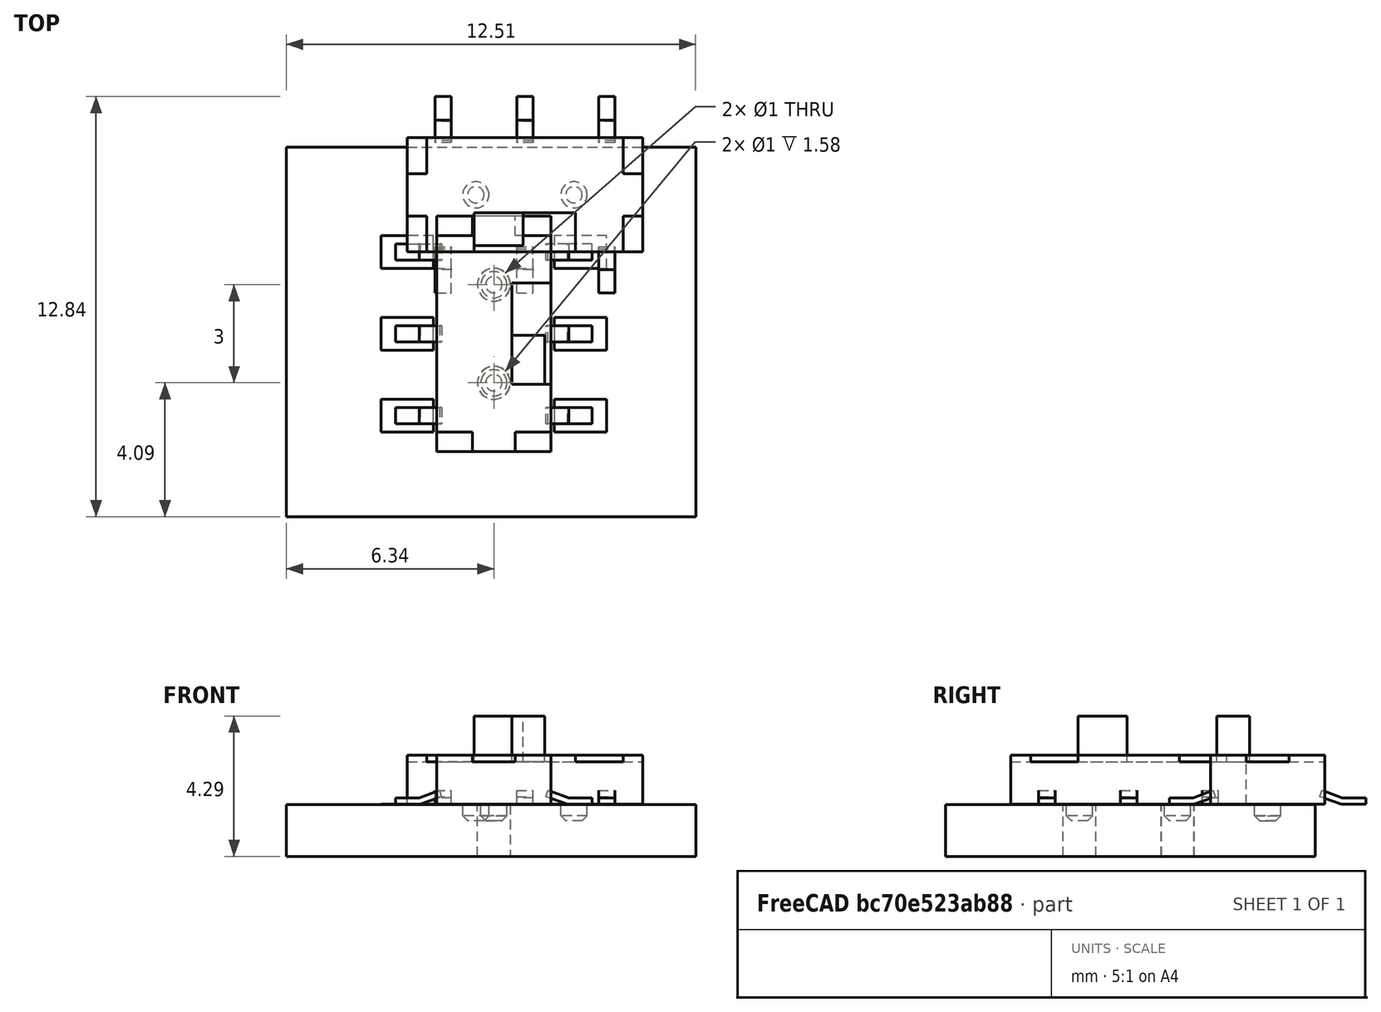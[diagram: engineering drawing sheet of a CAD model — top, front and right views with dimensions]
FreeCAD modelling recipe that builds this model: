
FCSTD DOCUMENT  (FreeCAD 0.18R16131 (Git))
Label: CK_AYZ0202AGRLC
License: All rights reserved
LicenseURL: http://en.wikipedia.org/wiki/All_rights_reserved
objects: Part::Box×26, Part::Feature×12, Part::Cut×11, Part::MultiFuse×6, Part::FeaturePython×6, Part::Cylinder×2, Part::Chamfer×2, App::Part×1, App::DocumentObjectGroup×1
note: 65 computed .brp shape members not serialized (recipe doc carries the construction recipe); baked Part::Feature solids carry a one-line shape summary decoded from their .brp

FEATURE [Part::Box] Box  label="Cube"
  AttacherType = Attacher::AttachEngine3D
  Height = 1.5
  Length = 7.2
  Width = 3.5
FEATURE [Part::Box] Box001  label="Cube001"
  AttacherType = Attacher::AttachEngine3D
  Height = 0.2
  Length = 0.5
  Placement = pos=(0,-1.25,0) rot=(0,0,1;0rad)
  Width = 0.75
FEATURE [Part::Box] Box002  label="Cube002"
  AttacherType = Attacher::AttachEngine3D
  Height = 0.2
  Length = 0.5
  Placement = pos=(0,-0.5,0) rot=(1,0,0;0.349066rad)
  Width = 0.7
FEATURE [Part::MultiFuse] Fusion  label="Pin 4"
  Placement = pos=(3.35,0,0) rot=(0,0,1;0rad)
  Shapes = -> [Box002,Box001]
FEATURE [Part::Box] Box003  label="Cube003"
  AttacherType = Attacher::AttachEngine3D
  Height = 0.2
  Length = 0.5
  Placement = pos=(0,-1.25,0) rot=(0,0,1;0rad)
  Width = 0.75
FEATURE [Part::Box] Box004  label="Cube004"
  AttacherType = Attacher::AttachEngine3D
  Height = 0.2
  Length = 0.5
  Placement = pos=(0,-0.5,0) rot=(1,0,0;0.349066rad)
  Width = 0.7
FEATURE [Part::MultiFuse] Fusion001  label="Pin 5"
  Placement = pos=(0.85,0,0) rot=(0,0,1;0rad)
  Shapes = -> [Box004,Box003]
FEATURE [Part::Box] Box005  label="Cube005"
  AttacherType = Attacher::AttachEngine3D
  Height = 0.2
  Length = 0.5
  Placement = pos=(0,-1.25,0) rot=(0,0,1;0rad)
  Width = 0.75
FEATURE [Part::Box] Box006  label="Cube006"
  AttacherType = Attacher::AttachEngine3D
  Height = 0.2
  Length = 0.5
  Placement = pos=(0,-0.5,0) rot=(1,0,0;0.349066rad)
  Width = 0.7
FEATURE [Part::MultiFuse] Fusion002  label="Pin 6"
  Placement = pos=(5.85,0,0) rot=(0,0,1;0rad)
  Shapes = -> [Box006,Box005]
FEATURE [Part::Box] Box007  label="Cube007"
  AttacherType = Attacher::AttachEngine3D
  Height = 0.2
  Length = 0.5
  Placement = pos=(0,-1.25,0) rot=(0,0,1;0rad)
  Width = 0.75
FEATURE [Part::Box] Box008  label="Cube008"
  AttacherType = Attacher::AttachEngine3D
  Height = 0.2
  Length = 0.5
  Placement = pos=(0,-0.5,0) rot=(1,0,0;0.349066rad)
  Width = 0.7
FEATURE [Part::MultiFuse] Fusion003  label="Pin 2"
  Placement = pos=(3.85,3.5,0) rot=(0,0,1;3.14159rad)
  Shapes = -> [Box008,Box007]
FEATURE [Part::Box] Box009  label="Cube009"
  AttacherType = Attacher::AttachEngine3D
  Height = 0.2
  Length = 0.5
  Placement = pos=(0,-1.25,0) rot=(0,0,1;0rad)
  Width = 0.75
FEATURE [Part::Box] Box010  label="Cube010"
  AttacherType = Attacher::AttachEngine3D
  Height = 0.2
  Length = 0.5
  Placement = pos=(0,-0.5,0) rot=(1,0,0;0.349066rad)
  Width = 0.7
FEATURE [Part::MultiFuse] Fusion004  label="Pin 1"
  Placement = pos=(1.35,3.5,0) rot=(0,0,1;3.14159rad)
  Shapes = -> [Box010,Box009]
FEATURE [Part::Box] Box011  label="Cube011"
  AttacherType = Attacher::AttachEngine3D
  Height = 0.2
  Length = 0.5
  Placement = pos=(0,-1.25,0) rot=(0,0,1;0rad)
  Width = 0.75
FEATURE [Part::Box] Box012  label="Cube012"
  AttacherType = Attacher::AttachEngine3D
  Height = 0.2
  Length = 0.5
  Placement = pos=(0,-0.5,0) rot=(1,0,0;0.349066rad)
  Width = 0.7
FEATURE [Part::MultiFuse] Fusion005  label="Pin 3"
  Placement = pos=(6.35,3.5,0) rot=(0,0,1;3.14159rad)
  Shapes = -> [Box012,Box011]
FEATURE [Part::Box] Box014  label="Cube014"
  AttacherType = Attacher::AttachEngine3D
  Height = 0.2
  Length = 0.6
  Placement = pos=(6.6,0,1.3) rot=(0,0,1;0rad)
  Width = 1.1
FEATURE [Part::Box] Box015  label="Cube015"
  AttacherType = Attacher::AttachEngine3D
  Height = 0.2
  Length = 0.6
  Placement = pos=(6.6,2.4,1.3) rot=(0,0,1;0rad)
  Width = 1.1
FEATURE [Part::Box] Box016  label="Cube016"
  AttacherType = Attacher::AttachEngine3D
  Height = 0.2
  Length = 0.6
  Placement = pos=(0,0,1.3) rot=(0,0,1;0rad)
  Width = 1.1
FEATURE [Part::Box] Box017  label="Cube017"
  AttacherType = Attacher::AttachEngine3D
  Height = 0.2
  Length = 0.6
  Placement = pos=(0,2.4,1.3) rot=(0,0,1;0rad)
  Width = 1.1
FEATURE [Part::Box] Box018  label="Cube018"
  AttacherType = Attacher::AttachEngine3D
  Height = 0.2
  Length = 3.1
  Placement = pos=(2.05,0,1.3) rot=(0,0,1;0rad)
  Width = 1.2
FEATURE [Part::Box] Box019  label="Cube019"
  AttacherType = Attacher::AttachEngine3D
  Height = 0.2
  Length = 7.2
  Placement = pos=(0,0,1.3) rot=(0,0,1;0rad)
  Width = 3.5
FEATURE [Part::Cut] Cut
  Base = -> Box019
  Tool = -> Box014
FEATURE [Part::Cut] Cut001
  Base = -> Cut
  Tool = -> Box015
FEATURE [Part::Cut] Cut002
  Base = -> Cut001
  Tool = -> Box016
FEATURE [Part::Cut] Cut003
  Base = -> Cut002
  Tool = -> Box017
FEATURE [Part::Cut] Cut004  label="Silver Top"
  Base = -> Cut003
  Tool = -> Box018
FEATURE [Part::Box] Box020  label="Cube020"
  AttacherType = Attacher::AttachEngine3D
  Height = 0.2
  Length = 0.6
  Placement = pos=(6.6,0,1.3) rot=(0,0,1;0rad)
  Width = 1.1
FEATURE [Part::Box] Box021  label="Cube021"
  AttacherType = Attacher::AttachEngine3D
  Height = 0.2
  Length = 0.6
  Placement = pos=(6.6,2.4,1.3) rot=(0,0,1;0rad)
  Width = 1.1
FEATURE [Part::Box] Box022  label="Cube022"
  AttacherType = Attacher::AttachEngine3D
  Height = 0.2
  Length = 0.6
  Placement = pos=(0,0,1.3) rot=(0,0,1;0rad)
  Width = 1.1
FEATURE [Part::Box] Box023  label="Cube023"
  AttacherType = Attacher::AttachEngine3D
  Height = 0.2
  Length = 0.6
  Placement = pos=(0,2.4,1.3) rot=(0,0,1;0rad)
  Width = 1.1
FEATURE [Part::Box] Box024  label="Cube024"
  AttacherType = Attacher::AttachEngine3D
  Height = 0.2
  Length = 3.1
  Placement = pos=(2.05,0,1.3) rot=(0,0,1;0rad)
  Width = 1.2
FEATURE [Part::Box] Box025  label="Cube025"
  AttacherType = Attacher::AttachEngine3D
  Height = 0.2
  Length = 7.2
  Placement = pos=(0,0,1.3) rot=(0,0,1;0rad)
  Width = 3.5
FEATURE [Part::Cut] Cut005
  Base = -> Box025
  Tool = -> Box020
FEATURE [Part::Cut] Cut009
  Base = -> Cut005
  Tool = -> Box021
FEATURE [Part::Cut] Cut006
  Base = -> Cut009
  Tool = -> Box022
FEATURE [Part::Cut] Cut008
  Base = -> Cut006
  Tool = -> Box023
FEATURE [Part::Cut] Cut007  label="Silver Top001"
  Base = -> Cut008
  Tool = -> Box024
FEATURE [Part::Cut] Cut010  label="Plastic Body"
  Base = -> Box
  Tool = -> Cut007
FEATURE [Part::Box] Box026  label="Cube026"
  AttacherType = Attacher::AttachEngine3D
  Height = 1.4
  Length = 1.5
  Placement = pos=(2.05,0.2,1.3) rot=(0,0,1;0rad)
  Width = 1
FEATURE [Part::Cylinder] Cylinder
  Angle = 360
  AttacherType = Attacher::AttachEngine3D
  Height = 0.5
  Placement = pos=(3.6,1.75,-0.5) rot=(0,0,1;0rad)
  Radius = 0.4
FEATURE [Part::Chamfer] Chamfer
  Base = -> Cylinder
  Edges = 1 edges r=0.15: [Edge3]
  Placement = pos=(-1.5,0,0) rot=(0,0,1;0rad)
FEATURE [Part::Cylinder] Cylinder001
  Angle = 360
  AttacherType = Attacher::AttachEngine3D
  Height = 0.5
  Placement = pos=(3.6,1.75,-0.5) rot=(0,0,1;0rad)
  Radius = 0.4
FEATURE [Part::Chamfer] Chamfer001
  Base = -> Cylinder001
  Edges = 1 edges r=0.15: [Edge3]
  Placement = pos=(1.5,0,0) rot=(0,0,1;0rad)
FEATURE [App::Part] Part
  Group = -> [Box001,Box002,Fusion,Box004,Box003,Fusion001,Box006,Box005,Fusion002,Box007,Box008,Fusion003,Box010,Box009,Fusion004,Box012,Box011,Fusion005,Cut,Cut002,Cut003,Cut001,Box014,Box015,Box016,Box017,Box018,Box019,Cut004,Cut007,Cut008,Cut009,Cut005,Cut006,Box,Box020,Box023,Box021,Box025,Box022,Box024,Cut010,Box026,Cylinder,Chamfer,Cylinder001,Chamfer001]
  Origin = -> Origin
FEATURE [Part::FeaturePython] FCrtYd_lines  label="FCrtYd"  # a2plus imported part (geometry in sourceFile) (typed FeaturePython)
  fixedPosition = true
FEATURE [Part::FeaturePython] FFab_lines  label="FFab"  # a2plus imported part (geometry in sourceFile) (typed FeaturePython)
  fixedPosition = true
FEATURE [Part::FeaturePython] Filk_lines  label="FrontSilk"  # a2plus imported part (geometry in sourceFile) (typed FeaturePython)
  fixedPosition = true
FEATURE [Part::FeaturePython] TopPads  # a2plus imported part (geometry in sourceFile) (typed FeaturePython)
  fixedPosition = true
FEATURE [Part::FeaturePython] THPs  label="PTHs"  # a2plus imported part (geometry in sourceFile) (typed FeaturePython)
  fixedPosition = true
FEATURE [Part::FeaturePython] newPCB  label="Pcb"  # a2plus imported part (geometry in sourceFile) (typed FeaturePython)
  fixedPosition = true
FEATURE [App::DocumentObjectGroup] Switch_Slide_SPDT_SMD_fp
  Group = -> [FCrtYd_lines,FFab_lines,Filk_lines,TopPads,THPs,newPCB]
FEATURE [Part::Feature] Fusion_cp  label="Pin 4_cp"
  Placement = pos=(3.35,0,0) rot=(0,0,1;0rad)
  shape: bbox 0.5 x 1.408 x 0.4274 mm, 12 faces (baked)
FEATURE [Part::Feature] Fusion001_cp  label="Pin 5_cp"
  Placement = pos=(0.85,0,0) rot=(0,0,1;0rad)
  shape: bbox 0.5 x 1.408 x 0.4274 mm, 12 faces (baked)
FEATURE [Part::Feature] Fusion002_cp  label="Pin 6_cp"
  Placement = pos=(5.85,0,0) rot=(0,0,1;0rad)
  shape: bbox 0.5 x 1.408 x 0.4274 mm, 12 faces (baked)
FEATURE [Part::Feature] Fusion003_cp  label="Pin 2_cp"
  Placement = pos=(3.85,3.5,0) rot=(0,0,1;3.14159rad)
  shape: bbox 0.5 x 1.408 x 0.4274 mm, 12 faces (baked)
FEATURE [Part::Feature] Fusion004_cp  label="Pin 1_cp"
  Placement = pos=(1.35,3.5,0) rot=(0,0,1;3.14159rad)
  shape: bbox 0.5 x 1.408 x 0.4274 mm, 12 faces (baked)
FEATURE [Part::Feature] Fusion005_cp  label="Pin 3_cp"
  Placement = pos=(6.35,3.5,0) rot=(0,0,1;3.14159rad)
  shape: bbox 0.5 x 1.408 x 0.4274 mm, 12 faces (baked)
FEATURE [Part::Feature] Cut004_cp  label="Silver Top_cp"
  shape: bbox 7.2 x 3.5 x 0.2 mm, 18 faces (baked)
FEATURE [Part::Feature] Cut010_cp  label="Plastic Body_cp"
  shape: bbox 7.2 x 3.5 x 1.5 mm, 22 faces (baked)
FEATURE [Part::Feature] Box026_cp  label="Cube026_cp"
  Placement = pos=(2.05,0.2,1.3) rot=(0,0,1;0rad)
  shape: bbox 1.5 x 1 x 1.4 mm, 6 faces (baked)
FEATURE [Part::Feature] Chamfer_cp
  Placement = pos=(-1.5,0,0) rot=(0,0,1;0rad)
  shape: bbox 0.8 x 0.8 x 0.5 mm, 4 faces (baked)
FEATURE [Part::Feature] Chamfer001_cp
  Placement = pos=(1.5,0,0) rot=(0,0,1;0rad)
  shape: bbox 0.8 x 0.8 x 0.5 mm, 4 faces (baked)
FEATURE [Part::Feature] Shape001  label="CK_AYZ0202AGRLC_cp"
  shape: bbox 6 x 7.2 x 3.2 mm, 126 faces, 11 solids (baked)
